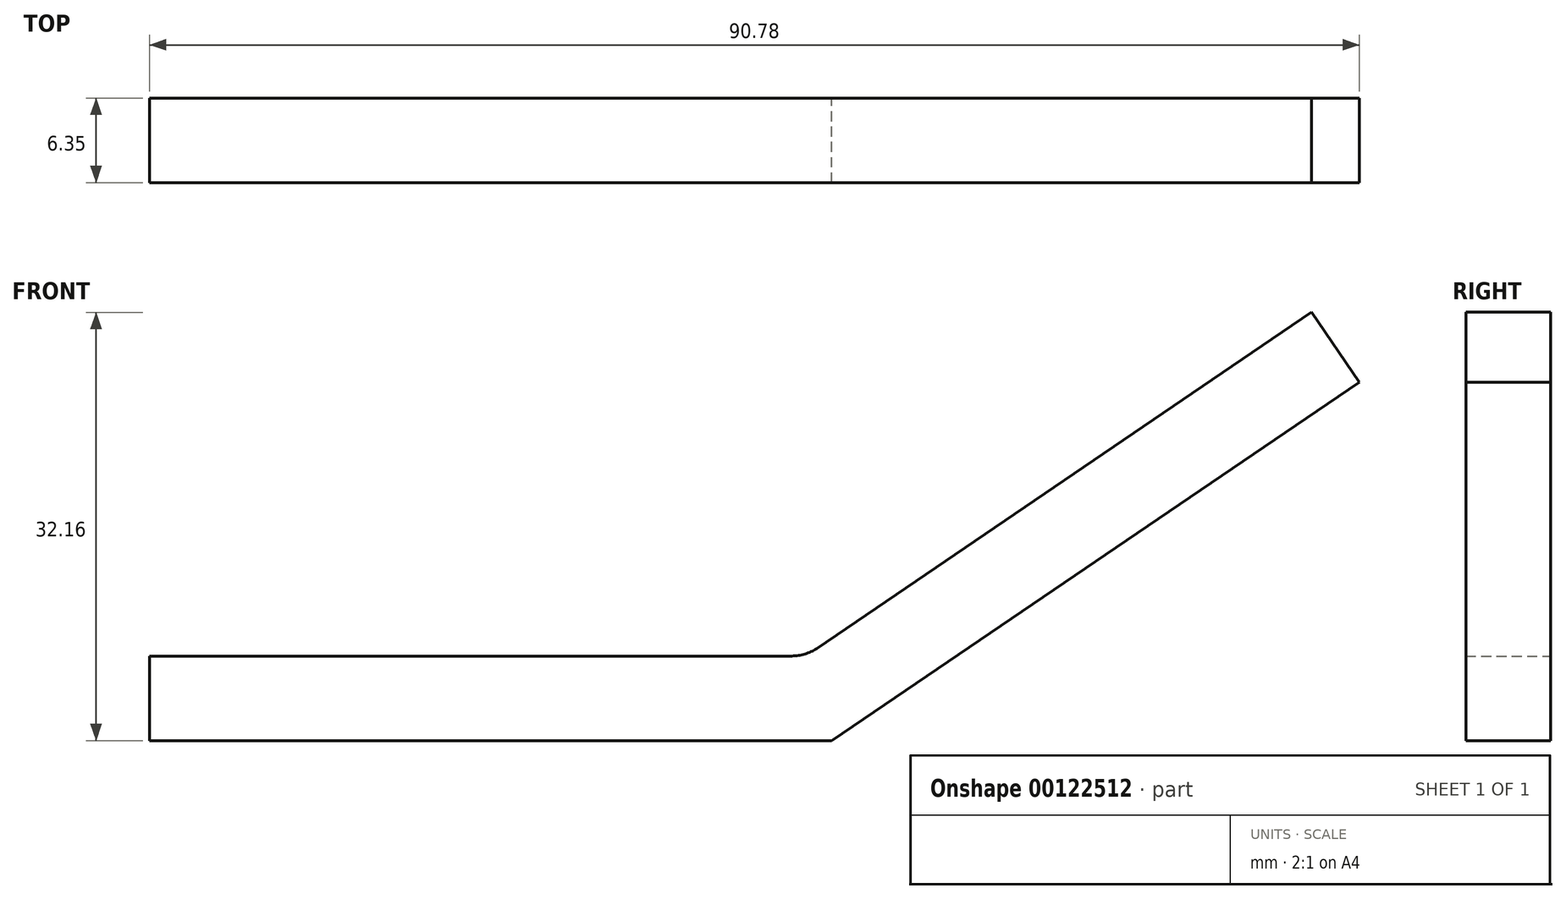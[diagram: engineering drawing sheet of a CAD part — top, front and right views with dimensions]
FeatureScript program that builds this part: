
annotation { "Feature Type Name" : "Feature", "Feature Type Description" : "" }
export const myFeature = defineFeature(function(context is Context, id is Id, definition is map)
    precondition{}
    {
        {
            var Q0;
            Q0=qCreatedBy(makeId("Front.planeOp"),FACE);
            var sketch = newSketch(context, id + "F0", { "sketchPlane" : qUnion([Q0])});
            skLineSegment(sketch, "E0", {"start": v(-51.18, 0) * mm, "end": v(0, 0) * mm});
            skLineSegment(sketch, "E1", {"start": v(0, 0) * mm, "end": v(39.6, 26.91) * mm});
            skLineSegment(sketch, "E2", {"start": v(39.6, 26.91) * mm, "end": v(36.03, 32.16) * mm});
            skLineSegment(sketch, "E3", {"start": v(36.03, 32.16) * mm, "end": v(-1.11, 6.92) * mm});
            skLineSegment(sketch, "E4", {"start": v(-2.97, 6.35) * mm, "end": v(-51.18, 6.35) * mm});
            skLineSegment(sketch, "E5", {"start": v(-51.18, 6.35) * mm, "end": v(-51.18, 0) * mm});
            skPoint(sketch, "E6.orphan", {"position": v(0, 7.68) * mm});
            skPoint(sketch, "E7.orphan", {"position": v(-0.2, 6.35) * mm});
            skPoint(sketch, "E8.visualSharp", {"position": v(-3.4, 6.35) * mm});
            skPoint(sketch, "E9.visualSharp", {"position": v(-1.95, 6.35) * mm});
            skArc(sketch, "E9.filletArc", {"start": v(-2.97, 6.35) * mm, "mid": v(-2, 6.5) * mm, "end": v(-1.11, 6.92) * mm});
            skSolve(sketch);
        }
        {
            var Q0;
            Q0 = qSketchRegion(id + "F0", true);
            extrude(context, id + "F1", {"entities" : qUnion([Q0]), "depth" : 6.35 * mm});
        }
    });
